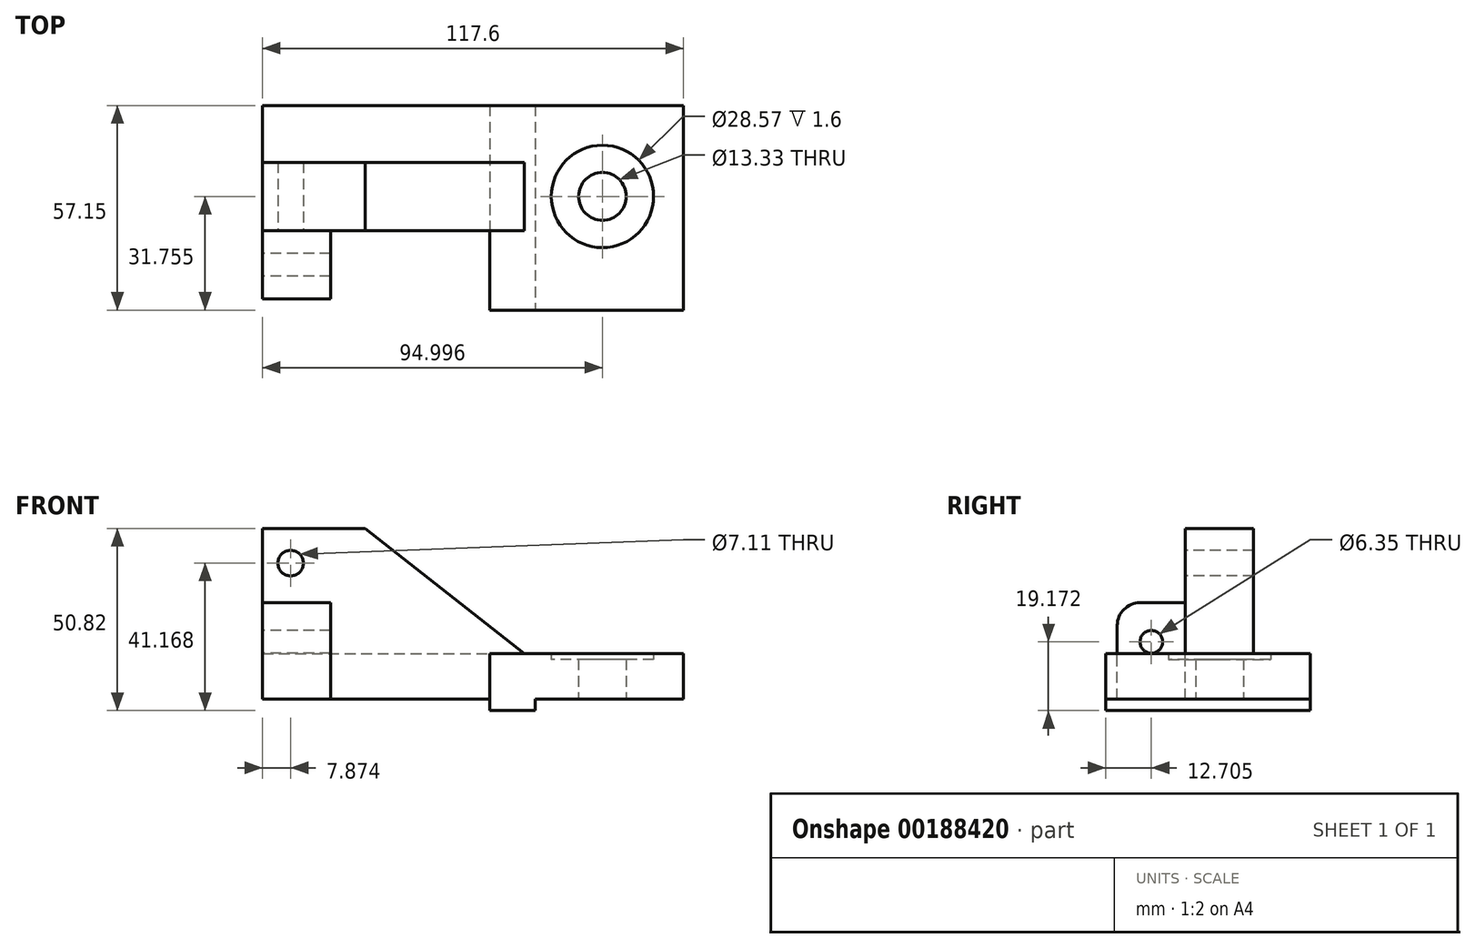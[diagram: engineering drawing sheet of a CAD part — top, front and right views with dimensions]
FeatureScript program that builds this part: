
annotation { "Feature Type Name" : "Feature", "Feature Type Description" : "" }
export const myFeature = defineFeature(function(context is Context, id is Id, definition is map)
    precondition{}
    {
        {
            var Q0;
            Q0=qCreatedBy(makeId("Front.planeOp"),FACE);
            var sketch = newSketch(context, id + "F0", { "sketchPlane" : qUnion([Q0])});
            skLineSegment(sketch, "E0", {"start": v(0, 0) * mm, "end": v(0, 47.65) * mm});
            skLineSegment(sketch, "E1", {"start": v(0, 47.65) * mm, "end": v(28.7, 47.65) * mm});
            skLineSegment(sketch, "E2", {"start": v(28.7, 47.65) * mm, "end": v(73.15, 12.7) * mm});
            skLineSegment(sketch, "E3", {"start": v(73.15, 12.7) * mm, "end": v(73.15, 0) * mm});
            skLineSegment(sketch, "E4", {"start": v(73.15, 0) * mm, "end": v(0, 0) * mm});
            skCircle(sketch, "E5", {"center": v(7.87, 38) * mm, "radius": 3.56 * mm});
            skSolve(sketch);
        }
        {
            var Q0;
            Q0=makeQuery(id+"F0.imprint","IMPRINT",FACE,{"disambiguationData":[TD([[makeQuery(id+"F0.imprint","IMPRINT",EDGE,{"derivedFrom":sQuery(id+"F0.wireOp",EDGE,"E0")}),-1.0]])]});
            extrude(context, id + "F1", {"entities" : qUnion([Q0]), "oppositeDirection" : true, "depth" : 19.05 * mm});
        }
        {
            var Q0;
            Q0=qCreatedBy(makeId("Right.planeOp"),FACE);
            var sketch = newSketch(context, id + "F2", { "sketchPlane" : qUnion([Q0])});
            skLineSegment(sketch, "E6.bottom", {"start": v(0, 0) * mm, "end": v(-19.05, 0) * mm});
            skLineSegment(sketch, "E6.top", {"start": v(0, 26.92) * mm, "end": v(-19.05, 26.92) * mm});
            skLineSegment(sketch, "E6.left", {"start": v(0, 0) * mm, "end": v(0, 26.92) * mm});
            skLineSegment(sketch, "E6.right", {"start": v(-19.05, 0) * mm, "end": v(-19.05, 26.92) * mm});
            skCircle(sketch, "E7", {"center": v(-9.53, 16) * mm, "radius": 3.18 * mm});
            skSolve(sketch);
        }
        {
            var Q0;
            Q0=makeQuery(id+"F2.imprint","IMPRINT",FACE,{"disambiguationData":[TD([[makeQuery(id+"F2.imprint","IMPRINT",EDGE,{"derivedFrom":sQuery(id+"F2.wireOp",EDGE,"E6.bottom")}),-1.0]])]});
            extrude(context, id + "F3", {"entities" : qUnion([Q0]), "operationType" : NewBodyOperationType.ADD, "depth" : 19.05 * mm});
        }
        {
            var Q0;
            Q0=makeQuery(id+"F3.opExtrude","SWEPT_EDGE",EDGE,{"disambiguationData":[OSD([sQuery(id+"F2.wireOp",EDGE,"E6.top"),sQuery(id+"F2.wireOp",EDGE,"E6.right")])]});
            fillet(context, id + "F4", {"entities" : qUnion([Q0]), "radius" : 6.35 * mm, "tangentPropagation" : true, "allowEdgeOverflow" : false});
        }
        {
            var Q0;
            Q0=qCreatedBy(makeId("Front.planeOp"),FACE);
            cPlane(context, id + "F5", {"entities" : qUnion([Q0]), "cplaneType" : CPlaneType.OFFSET, "offset" : 19.05 * mm, "oppositeDirection" : true, "width" : 152.4 * mm, "height" : 152.4 * mm});
        }
        {
            var Q0;
            Q0=qCreatedBy(id+"F5.planeOp",FACE);
            var sketch = newSketch(context, id + "F6", { "sketchPlane" : qUnion([Q0])});
            skLineSegment(sketch, "E8.bottom", {"start": v(0, 0) * mm, "end": v(73.15, 0) * mm});
            skLineSegment(sketch, "E8.top", {"start": v(0, 12.7) * mm, "end": v(73.15, 12.7) * mm});
            skLineSegment(sketch, "E8.left", {"start": v(0, 0) * mm, "end": v(0, 12.7) * mm});
            skLineSegment(sketch, "E8.right", {"start": v(73.15, 0) * mm, "end": v(73.15, 12.7) * mm});
            skSolve(sketch);
        }
        {
            var Q0;
            Q0=makeQuery(id+"F6.imprint","IMPRINT",FACE,{"disambiguationData":[TD([[makeQuery(id+"F6.imprint","IMPRINT",EDGE,{"derivedFrom":sQuery(id+"F6.wireOp",EDGE,"E8.bottom")}),1.0]])]});
            extrude(context, id + "F7", {"entities" : qUnion([Q0]), "operationType" : NewBodyOperationType.ADD, "oppositeDirection" : true, "depth" : 15.88 * mm});
        }
        {
            var Q0;
            Q0=qCreatedBy(makeId("Top.planeOp"),FACE);
            var sketch = newSketch(context, id + "F8", { "sketchPlane" : qUnion([Q0])});
            skLineSegment(sketch, "E9", {"start": v(0, 0) * mm, "end": v(73.15, 0) * mm});
            skLineSegment(sketch, "E10", {"start": v(73.15, 0) * mm, "end": v(73.15, 34.93) * mm});
            skLineSegment(sketch, "E11.bottom", {"start": v(73.15, 34.93) * mm, "end": v(117.6, 34.93) * mm});
            skLineSegment(sketch, "E11.top", {"start": v(73.15, -22.22) * mm, "end": v(117.6, -22.22) * mm});
            skLineSegment(sketch, "E11.left", {"start": v(73.15, 34.93) * mm, "end": v(73.15, -22.22) * mm});
            skLineSegment(sketch, "E11.right", {"start": v(117.6, 34.93) * mm, "end": v(117.6, -22.22) * mm});
            skLineSegment(sketch, "E12", {"start": v(117.6, -22.22) * mm, "end": v(117.6, 9.53) * mm});
            skLineSegment(sketch, "E13", {"start": v(117.6, 9.53) * mm, "end": v(95, 9.53) * mm});
            skPoint(sketch, "E14", {"position": v(95, 9.53) * mm});
            skCircle(sketch, "E15", {"center": v(95, 9.53) * mm, "radius": 6.67 * mm});
            skCircle(sketch, "E16", {"center": v(95, 9.53) * mm, "radius": 14.29 * mm});
            skSolve(sketch);
        }
        {
            var Q0;
            {var subQ3=sQuery(id+"F8.wireOp",EDGE,"E11.bottom");Q0=makeQuery(id+"F8.imprint","IMPRINT",FACE,{"disambiguationData":[TD([[makeQuery(id+"F8.imprint","IMPRINT",EDGE,{"derivedFrom":subQ3}),-1.0]])]});}
            extrude(context, id + "F9", {"entities" : qUnion([Q0]), "operationType" : NewBodyOperationType.ADD, "depth" : 12.7 * mm});
        }
        {
            var Q0;
            Q0=makeQuery(id+"F8.imprint","IMPRINT",FACE,{"disambiguationData":[TD([[makeQuery(id+"F8.imprint","IMPRINT",EDGE,{"derivedFrom":sQuery(id+"F8.wireOp",EDGE,"E15")}),-1.0]])]});
            extrude(context, id + "F10", {"entities" : qUnion([Q0]), "operationType" : NewBodyOperationType.ADD, "depth" : 11.1 * mm});
        }
        {
            var Q0;
            Q0=qCreatedBy(makeId("Top.planeOp"),FACE);
            var sketch = newSketch(context, id + "F11", { "sketchPlane" : qUnion([Q0])});
            skLineSegment(sketch, "E17", {"start": v(0, 0) * mm, "end": v(63.5, 0) * mm});
            skLineSegment(sketch, "E18", {"start": v(0, 0) * mm, "end": v(0, 34.93) * mm});
            skLineSegment(sketch, "E19.bottom", {"start": v(63.5, 34.93) * mm, "end": v(76.2, 34.93) * mm});
            skLineSegment(sketch, "E19.top", {"start": v(63.5, -22.23) * mm, "end": v(76.2, -22.23) * mm});
            skLineSegment(sketch, "E19.left", {"start": v(63.5, 34.93) * mm, "end": v(63.5, -22.23) * mm});
            skLineSegment(sketch, "E19.right", {"start": v(76.2, 34.93) * mm, "end": v(76.2, -22.23) * mm});
            skSolve(sketch);
        }
        {
            var Q0;
            {var subQ3=sQuery(id+"F11.wireOp",EDGE,"E19.bottom");Q0=makeQuery(id+"F11.imprint","IMPRINT",FACE,{"disambiguationData":[TD([[makeQuery(id+"F11.imprint","IMPRINT",EDGE,{"derivedFrom":subQ3}),-1.0]])]});}
            extrude(context, id + "F12", {"entities" : qUnion([Q0]), "operationType" : NewBodyOperationType.ADD, "oppositeDirection" : true, "depth" : 3.17 * mm});
        }
        {
            var Q0;
            Q0=makeQuery(id+"F12.opExtrude","CAP_FACE",FACE,{"disambiguationData":[OSD([sQuery(id+"F11.wireOp",EDGE,"E19.bottom"),sQuery(id+"F11.wireOp",EDGE,"E19.top"),sQuery(id+"F11.wireOp",EDGE,"E19.left"),sQuery(id+"F11.wireOp",EDGE,"E19.right")])],"isStart":false});
            extrude(context, id + "F13", {"entities" : qUnion([Q0]), "operationType" : NewBodyOperationType.ADD, "oppositeDirection" : true, "depth" : 15.88 * mm});
        }
    });
